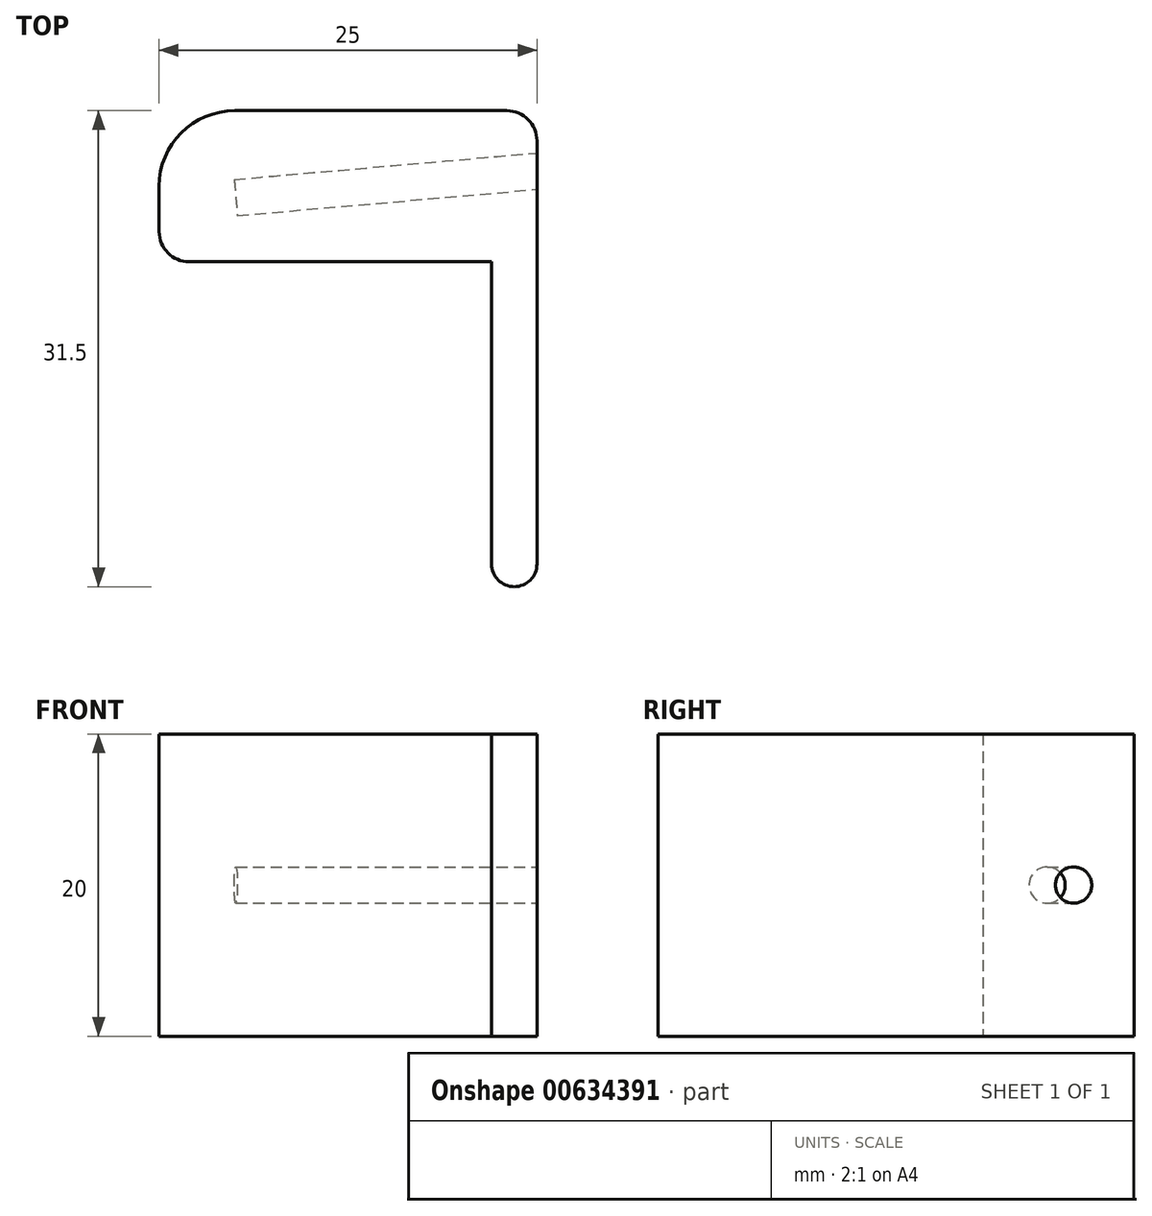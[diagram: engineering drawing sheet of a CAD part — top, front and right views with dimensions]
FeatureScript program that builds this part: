
annotation { "Feature Type Name" : "Feature", "Feature Type Description" : "" }
export const myFeature = defineFeature(function(context is Context, id is Id, definition is map)
    precondition{}
    {
        {
            var Q0;
            Q0=qCreatedBy(makeId("Top.planeOp"),FACE);
            var sketch = newSketch(context, id + "F0", { "sketchPlane" : qUnion([Q0])});
            skLineSegment(sketch, "E0", {"start": v(0, 0) * mm, "end": v(-22, 0) * mm});
            skLineSegment(sketch, "E1", {"start": v(-22, 0) * mm, "end": v(-22, 10) * mm});
            skLineSegment(sketch, "E2", {"start": v(-22, 10) * mm, "end": v(3, 10) * mm});
            skLineSegment(sketch, "E3", {"start": v(3, 10) * mm, "end": v(3, -20) * mm});
            skLineSegment(sketch, "E4", {"start": v(3, -20) * mm, "end": v(0, -20) * mm});
            skLineSegment(sketch, "E5", {"start": v(0, -20) * mm, "end": v(0, 0) * mm});
            skArc(sketch, "E6", {"start": v(0, -20) * mm, "mid": v(1.5, -21.5) * mm, "end": v(3, -20) * mm});
            skSolve(sketch);
        }
        {
            var Q0;
            Q0=makeQuery(id+"F0.imprint","IMPRINT",FACE,{"disambiguationData":[TD([[makeQuery(id+"F0.imprint","IMPRINT",EDGE,{"derivedFrom":sQuery(id+"F0.wireOp",EDGE,"E0")}),-1.0]])]});
            var Q1;
            Q1=makeQuery(id+"F0.imprint","IMPRINT",FACE,{"disambiguationData":[TD([[makeQuery(id+"F0.imprint","IMPRINT",EDGE,{"derivedFrom":sQuery(id+"F0.wireOp",EDGE,"E4")}),1.0]])]});
            extrude(context, id + "F1", {"entities" : qUnion([Q0, Q1]), "depth" : 20 * mm, "offsetDistance" : 25 * mm, "symmetric" : true});
        }
        {
            var Q0;
            Q0=qCreatedBy(makeId("Top.planeOp"),FACE);
            var sketch = newSketch(context, id + "F2", { "sketchPlane" : qUnion([Q0])});
            skLineSegment(sketch, "E7.0", {"start": v(3, 6) * mm, "end": v(3, -20) * mm});
            skLineSegment(sketch, "E8", {"start": v(-16.92, 4.26) * mm, "end": v(7.98, 6.44) * mm});
            skLineSegment(sketch, "E9", {"start": v(-16.92, 4.26) * mm, "end": v(-17.03, 5.45) * mm});
            skLineSegment(sketch, "E10", {"start": v(-17.03, 5.45) * mm, "end": v(7.88, 7.63) * mm});
            skLineSegment(sketch, "E11", {"start": v(7.88, 7.63) * mm, "end": v(7.98, 6.44) * mm});
            skPoint(sketch, "E12.0", {"position": v(0, 0) * mm});
            skPoint(sketch, "E13.0", {"position": v(3, 10) * mm});
            skSolve(sketch);
        }
        {
            var Q0;
            {var subQ0=sQuery(id+"F2.wireOp",EDGE,"E9");Q0=makeQuery(id+"F2.imprint","IMPRINT",FACE,{"disambiguationData":[TD([[makeQuery(id+"F2.imprint","IMPRINT",EDGE,{"derivedFrom":subQ0}),-1.0]])]});}
            var Q1;
            Q1=sQuery(id+"F2.wireOp",EDGE,"E8");
            revolve(context, id + "F3", {"operationType" : NewBodyOperationType.REMOVE, "surfaceOperationType" : NewSurfaceOperationType.NEW, "entities" : qUnion([Q0]), "axis" : qUnion([Q1]), "revolveType" : RevolveType.FULL, "oppositeDirection" : true});
        }
        {
            var Q0;
            Q0=makeQuery(id+"F1.opExtrude","SWEPT_EDGE",EDGE,{"disambiguationData":[OSD([sQuery(id+"F0.wireOp",EDGE,"E1"),sQuery(id+"F0.wireOp",EDGE,"E2")])]});
            fillet(context, id + "F4", {"entities" : qUnion([Q0]), "tangentPropagation" : true, "radius" : 5 * mm, "defaultsChanged" : false, "vertexSettings" : [], "allowEdgeOverflow" : false});
        }
        {
            var Q0;
            Q0=makeQuery(id+"F1.opExtrude","SWEPT_EDGE",EDGE,{"disambiguationData":[OSD([sQuery(id+"F0.wireOp",EDGE,"E2"),sQuery(id+"F0.wireOp",EDGE,"E3")])]});
            var Q1;
            Q1=makeQuery(id+"F1.opExtrude","SWEPT_EDGE",EDGE,{"disambiguationData":[OSD([sQuery(id+"F0.wireOp",EDGE,"E0"),sQuery(id+"F0.wireOp",EDGE,"E1")])]});
            fillet(context, id + "F5", {"entities" : qUnion([Q0, Q1]), "tangentPropagation" : true, "radius" : 2 * mm, "defaultsChanged" : false, "vertexSettings" : [], "allowEdgeOverflow" : false});
        }
    });
